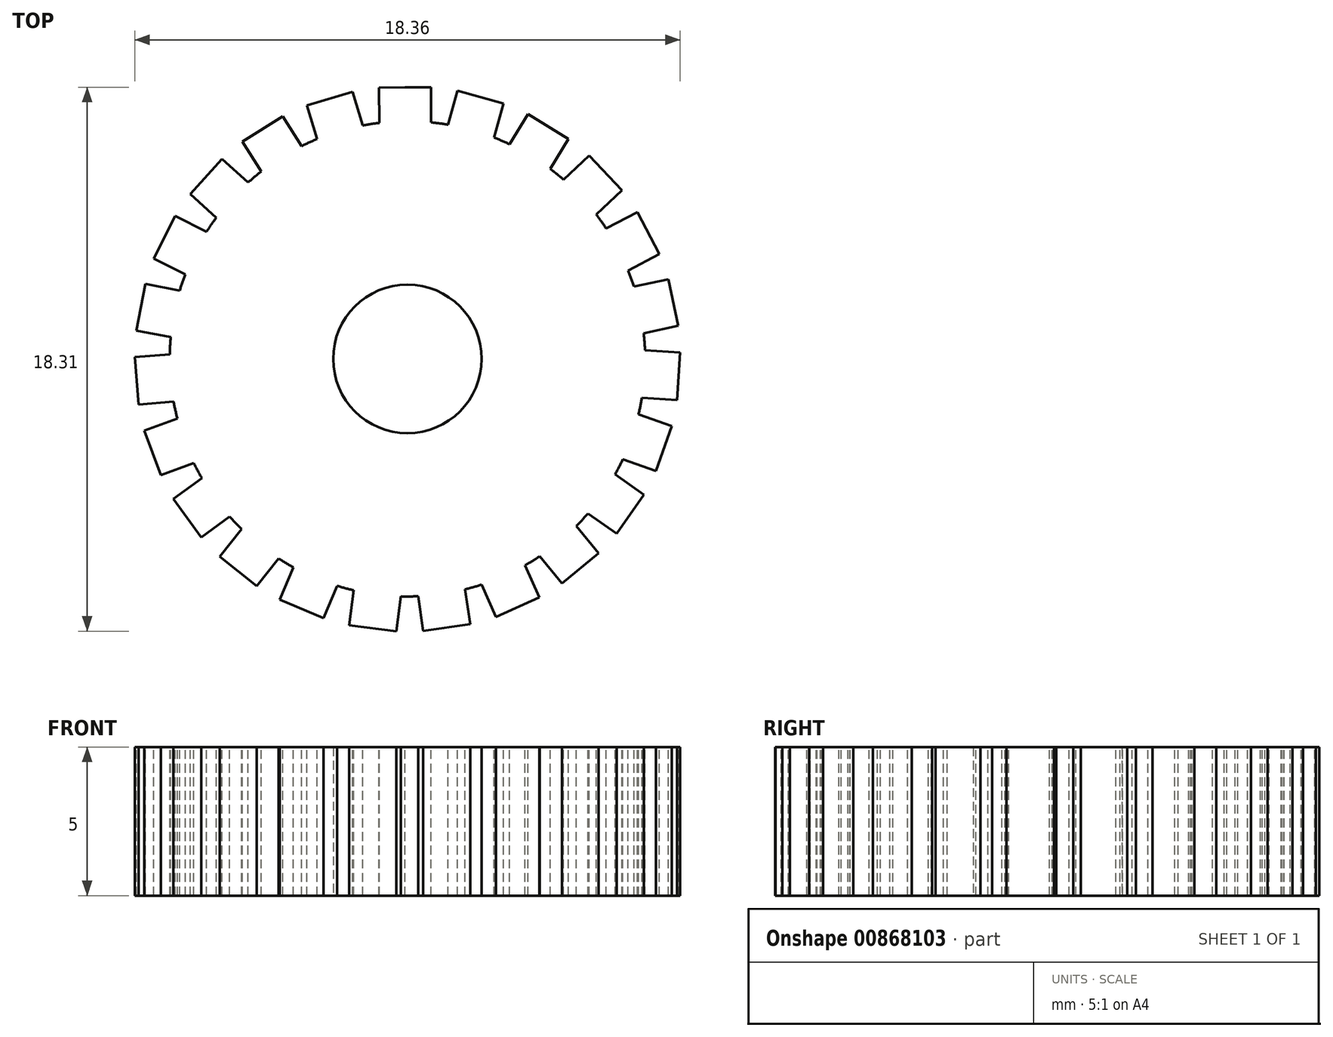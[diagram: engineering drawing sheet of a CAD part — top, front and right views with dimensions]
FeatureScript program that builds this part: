
annotation { "Feature Type Name" : "Feature", "Feature Type Description" : "" }
export const myFeature = defineFeature(function(context is Context, id is Id, definition is map)
    precondition{}
    {
        {
            var Q0;
            Q0=qCreatedBy(makeId("Top.planeOp"),FACE);
            var sketch = newSketch(context, id + "F0", { "sketchPlane" : qUnion([Q0])});
            skCircle(sketch, "E0", {"center": v(0, 0) * mm, "radius": 8 * mm});
            skCircle(sketch, "E1", {"center": v(0, 0) * mm, "radius": 2.5 * mm});
            skSolve(sketch);
        }
        {
            var Q0;
            Q0=makeQuery(id+"F0.imprint","IMPRINT",FACE,{"disambiguationData":[TD([[makeQuery(id+"F0.imprint","IMPRINT",EDGE,{"derivedFrom":sQuery(id+"F0.wireOp",EDGE,"E0")}),1.0]])]});
            extrude(context, id + "F1", {"entities" : qUnion([Q0]), "depth" : 5 * mm, "offsetDistance" : 25 * mm});
        }
        {
            var Q0;
            Q0=makeQuery(id+"F1.opExtrude","CAP_FACE",FACE,{"disambiguationData":[OSD([sQuery(id+"F0.wireOp",EDGE,"E0"),sQuery(id+"F0.wireOp",EDGE,"E1")])],"isStart":false});
            var sketch = newSketch(context, id + "F2", { "sketchPlane" : qUnion([Q0])});
            skLineSegment(sketch, "E2.bottom", {"start": v(-0.8, 9.14) * mm, "end": v(0.8, 9.14) * mm});
            skLineSegment(sketch, "E2.top", {"start": v(-0.8, 7.05) * mm, "end": v(0.8, 7.05) * mm});
            skLineSegment(sketch, "E2.right", {"start": v(0.8, 9.14) * mm, "end": v(0.8, 7.05) * mm});
            skLineSegment(sketch, "E3.1.0", {"start": v(3.23, 8.6) * mm, "end": v(2.67, 6.57) * mm});
            skLineSegment(sketch, "E3.1.1", {"start": v(1.69, 9.02) * mm, "end": v(3.23, 8.6) * mm});
            skLineSegment(sketch, "E3.1.2", {"start": v(1.69, 9.02) * mm, "end": v(1.13, 7) * mm});
            skLineSegment(sketch, "E3.1.3", {"start": v(1.13, 7) * mm, "end": v(2.67, 6.57) * mm});
            skLineSegment(sketch, "E3.2.0", {"start": v(5.42, 7.4) * mm, "end": v(4.34, 5.61) * mm});
            skLineSegment(sketch, "E3.2.1", {"start": v(4.06, 8.23) * mm, "end": v(5.42, 7.4) * mm});
            skLineSegment(sketch, "E3.2.2", {"start": v(4.06, 8.23) * mm, "end": v(2.97, 6.44) * mm});
            skLineSegment(sketch, "E3.2.3", {"start": v(2.97, 6.44) * mm, "end": v(4.34, 5.61) * mm});
            skLineSegment(sketch, "E3.3.0", {"start": v(7.22, 5.67) * mm, "end": v(5.69, 4.24) * mm});
            skLineSegment(sketch, "E3.3.1", {"start": v(6.12, 6.84) * mm, "end": v(7.22, 5.67) * mm});
            skLineSegment(sketch, "E3.3.2", {"start": v(6.12, 6.84) * mm, "end": v(4.6, 5.4) * mm});
            skLineSegment(sketch, "E3.3.3", {"start": v(4.6, 5.4) * mm, "end": v(5.69, 4.24) * mm});
            skLineSegment(sketch, "E3.4.0", {"start": v(8.48, 3.52) * mm, "end": v(6.62, 2.55) * mm});
            skLineSegment(sketch, "E3.4.1", {"start": v(7.74, 4.94) * mm, "end": v(8.48, 3.52) * mm});
            skLineSegment(sketch, "E3.4.2", {"start": v(7.74, 4.94) * mm, "end": v(5.88, 3.97) * mm});
            skLineSegment(sketch, "E3.4.3", {"start": v(5.88, 3.97) * mm, "end": v(6.62, 2.55) * mm});
            skLineSegment(sketch, "E3.5.0", {"start": v(9.11, 1.11) * mm, "end": v(7.06, 0.68) * mm});
            skLineSegment(sketch, "E3.5.1", {"start": v(8.78, 2.68) * mm, "end": v(9.11, 1.11) * mm});
            skLineSegment(sketch, "E3.5.2", {"start": v(8.78, 2.68) * mm, "end": v(6.73, 2.24) * mm});
            skLineSegment(sketch, "E3.5.3", {"start": v(6.73, 2.24) * mm, "end": v(7.06, 0.68) * mm});
            skLineSegment(sketch, "E3.6.0", {"start": v(9.07, -1.38) * mm, "end": v(6.98, -1.25) * mm});
            skLineSegment(sketch, "E3.6.1", {"start": v(9.18, 0.22) * mm, "end": v(9.07, -1.38) * mm});
            skLineSegment(sketch, "E3.6.2", {"start": v(9.18, 0.22) * mm, "end": v(7.08, 0.35) * mm});
            skLineSegment(sketch, "E3.6.3", {"start": v(7.08, 0.35) * mm, "end": v(6.98, -1.25) * mm});
            skLineSegment(sketch, "E3.7.0", {"start": v(8.37, -3.77) * mm, "end": v(6.39, -3.08) * mm});
            skLineSegment(sketch, "E3.7.1", {"start": v(8.9, -2.26) * mm, "end": v(8.37, -3.77) * mm});
            skLineSegment(sketch, "E3.7.2", {"start": v(8.9, -2.26) * mm, "end": v(6.92, -1.57) * mm});
            skLineSegment(sketch, "E3.7.3", {"start": v(6.92, -1.57) * mm, "end": v(6.39, -3.08) * mm});
            skLineSegment(sketch, "E3.8.0", {"start": v(7.04, -5.88) * mm, "end": v(5.32, -4.68) * mm});
            skLineSegment(sketch, "E3.8.1", {"start": v(7.96, -4.57) * mm, "end": v(7.04, -5.88) * mm});
            skLineSegment(sketch, "E3.8.2", {"start": v(7.96, -4.57) * mm, "end": v(6.24, -3.37) * mm});
            skLineSegment(sketch, "E3.8.3", {"start": v(6.24, -3.37) * mm, "end": v(5.32, -4.68) * mm});
            skLineSegment(sketch, "E3.9.0", {"start": v(5.2, -7.56) * mm, "end": v(3.87, -5.94) * mm});
            skLineSegment(sketch, "E3.9.1", {"start": v(6.44, -6.54) * mm, "end": v(5.2, -7.56) * mm});
            skLineSegment(sketch, "E3.9.2", {"start": v(6.44, -6.54) * mm, "end": v(5.1, -4.93) * mm});
            skLineSegment(sketch, "E3.9.3", {"start": v(5.1, -4.93) * mm, "end": v(3.87, -5.94) * mm});
            skLineSegment(sketch, "E3.10.0", {"start": v(2.98, -8.68) * mm, "end": v(2.12, -6.77) * mm});
            skLineSegment(sketch, "E3.10.1", {"start": v(4.44, -8.03) * mm, "end": v(2.98, -8.68) * mm});
            skLineSegment(sketch, "E3.10.2", {"start": v(4.44, -8.03) * mm, "end": v(3.59, -6.12) * mm});
            skLineSegment(sketch, "E3.10.3", {"start": v(3.59, -6.12) * mm, "end": v(2.12, -6.77) * mm});
            skLineSegment(sketch, "E3.11.0", {"start": v(0.53, -9.16) * mm, "end": v(0.23, -7.09) * mm});
            skLineSegment(sketch, "E3.11.1", {"start": v(2.11, -8.93) * mm, "end": v(0.53, -9.16) * mm});
            skLineSegment(sketch, "E3.11.2", {"start": v(2.11, -8.93) * mm, "end": v(1.8, -6.86) * mm});
            skLineSegment(sketch, "E3.11.3", {"start": v(1.8, -6.86) * mm, "end": v(0.23, -7.09) * mm});
            skLineSegment(sketch, "E3.12.0", {"start": v(-1.96, -8.97) * mm, "end": v(-1.69, -6.89) * mm});
            skLineSegment(sketch, "E3.12.1", {"start": v(-0.37, -9.17) * mm, "end": v(-1.96, -8.97) * mm});
            skLineSegment(sketch, "E3.12.2", {"start": v(-0.37, -9.17) * mm, "end": v(-0.1, -7.1) * mm});
            skLineSegment(sketch, "E3.12.3", {"start": v(-0.1, -7.1) * mm, "end": v(-1.69, -6.89) * mm});
            skLineSegment(sketch, "E3.13.0", {"start": v(-4.3, -8.11) * mm, "end": v(-3.48, -6.18) * mm});
            skLineSegment(sketch, "E3.13.1", {"start": v(-2.82, -8.73) * mm, "end": v(-4.3, -8.11) * mm});
            skLineSegment(sketch, "E3.13.2", {"start": v(-2.82, -8.73) * mm, "end": v(-2, -6.8) * mm});
            skLineSegment(sketch, "E3.13.3", {"start": v(-2, -6.8) * mm, "end": v(-3.48, -6.18) * mm});
            skLineSegment(sketch, "E3.14.0", {"start": v(-6.32, -6.66) * mm, "end": v(-5.01, -5.01) * mm});
            skLineSegment(sketch, "E3.14.1", {"start": v(-5.07, -7.65) * mm, "end": v(-6.32, -6.66) * mm});
            skLineSegment(sketch, "E3.14.2", {"start": v(-5.07, -7.65) * mm, "end": v(-3.76, -6.01) * mm});
            skLineSegment(sketch, "E3.14.3", {"start": v(-3.76, -6.01) * mm, "end": v(-5.01, -5.01) * mm});
            skLineSegment(sketch, "E3.15.0", {"start": v(-7.88, -4.7) * mm, "end": v(-6.18, -3.48) * mm});
            skLineSegment(sketch, "E3.15.1", {"start": v(-6.94, -6) * mm, "end": v(-7.88, -4.7) * mm});
            skLineSegment(sketch, "E3.15.2", {"start": v(-6.94, -6) * mm, "end": v(-5.24, -4.78) * mm});
            skLineSegment(sketch, "E3.15.3", {"start": v(-5.24, -4.78) * mm, "end": v(-6.18, -3.48) * mm});
            skLineSegment(sketch, "E3.16.0", {"start": v(-8.86, -2.42) * mm, "end": v(-6.89, -1.69) * mm});
            skLineSegment(sketch, "E3.16.1", {"start": v(-8.3, -3.92) * mm, "end": v(-8.86, -2.42) * mm});
            skLineSegment(sketch, "E3.16.2", {"start": v(-8.3, -3.92) * mm, "end": v(-6.33, -3.2) * mm});
            skLineSegment(sketch, "E3.16.3", {"start": v(-6.33, -3.2) * mm, "end": v(-6.89, -1.69) * mm});
            skLineSegment(sketch, "E3.17.0", {"start": v(-9.18, 0.06) * mm, "end": v(-7.09, 0.23) * mm});
            skLineSegment(sketch, "E3.17.1", {"start": v(-9.05, -1.54) * mm, "end": v(-9.18, 0.06) * mm});
            skLineSegment(sketch, "E3.17.2", {"start": v(-9.05, -1.54) * mm, "end": v(-6.96, -1.37) * mm});
            skLineSegment(sketch, "E3.17.3", {"start": v(-6.96, -1.37) * mm, "end": v(-7.09, 0.23) * mm});
            skLineSegment(sketch, "E3.18.0", {"start": v(-8.83, 2.52) * mm, "end": v(-6.77, 2.12) * mm});
            skLineSegment(sketch, "E3.18.1", {"start": v(-9.13, 0.95) * mm, "end": v(-8.83, 2.52) * mm});
            skLineSegment(sketch, "E3.18.2", {"start": v(-9.13, 0.95) * mm, "end": v(-7.07, 0.55) * mm});
            skLineSegment(sketch, "E3.18.3", {"start": v(-7.07, 0.55) * mm, "end": v(-6.77, 2.12) * mm});
            skLineSegment(sketch, "E3.19.0", {"start": v(-7.82, 4.8) * mm, "end": v(-5.94, 3.87) * mm});
            skLineSegment(sketch, "E3.19.1", {"start": v(-8.54, 3.37) * mm, "end": v(-7.82, 4.8) * mm});
            skLineSegment(sketch, "E3.19.2", {"start": v(-8.54, 3.37) * mm, "end": v(-6.66, 2.44) * mm});
            skLineSegment(sketch, "E3.19.3", {"start": v(-6.66, 2.44) * mm, "end": v(-5.94, 3.87) * mm});
            skLineSegment(sketch, "E3.20.0", {"start": v(-6.24, 6.73) * mm, "end": v(-4.68, 5.32) * mm});
            skLineSegment(sketch, "E3.20.1", {"start": v(-7.31, 5.55) * mm, "end": v(-6.24, 6.73) * mm});
            skLineSegment(sketch, "E3.20.2", {"start": v(-7.31, 5.55) * mm, "end": v(-5.76, 4.14) * mm});
            skLineSegment(sketch, "E3.20.3", {"start": v(-5.76, 4.14) * mm, "end": v(-4.68, 5.32) * mm});
            skLineSegment(sketch, "E3.21.0", {"start": v(-4.2, 8.16) * mm, "end": v(-3.08, 6.39) * mm});
            skLineSegment(sketch, "E3.21.1", {"start": v(-5.55, 7.3) * mm, "end": v(-4.2, 8.16) * mm});
            skLineSegment(sketch, "E3.21.2", {"start": v(-5.55, 7.3) * mm, "end": v(-4.43, 5.53) * mm});
            skLineSegment(sketch, "E3.21.3", {"start": v(-4.43, 5.53) * mm, "end": v(-3.08, 6.39) * mm});
            skLineSegment(sketch, "E3.22.0", {"start": v(-1.85, 9) * mm, "end": v(-1.25, 6.98) * mm});
            skLineSegment(sketch, "E3.22.1", {"start": v(-3.38, 8.53) * mm, "end": v(-1.85, 9) * mm});
            skLineSegment(sketch, "E3.22.2", {"start": v(-3.38, 8.53) * mm, "end": v(-2.78, 6.52) * mm});
            skLineSegment(sketch, "E3.22.3", {"start": v(-2.78, 6.52) * mm, "end": v(-1.25, 6.98) * mm});
            skLineSegment(sketch, "E3.23.1", {"start": v(-0.96, 9.13) * mm, "end": v(0.64, 9.16) * mm});
            skLineSegment(sketch, "E3.23.2", {"start": v(-0.96, 9.13) * mm, "end": v(-0.92, 7.03) * mm});
            skLineSegment(sketch, "E3.23.3", {"start": v(-0.92, 7.03) * mm, "end": v(0.68, 7.06) * mm});
            skPoint(sketch, "E3.center", {"position": v(0, 0) * mm});
            skLineSegment(sketch, "E3.anchor1", {"start": v(0, 0) * mm, "end": v(-0.8, 7.05) * mm, "construction": true});
            skLineSegment(sketch, "E3.anchor2", {"start": v(0, 0) * mm, "end": v(-0.92, 7.03) * mm, "construction": true});
            skSolve(sketch);
        }
        {
            var Q0;
            {var subQ0=sQuery(id+"F2.wireOp",EDGE,"E3.19.1");Q0=makeQuery(id+"F2.imprint","IMPRINT",FACE,{"disambiguationData":[TD([[makeQuery(id+"F2.imprint","IMPRINT",EDGE,{"derivedFrom":subQ0}),-1.0]])]});}
            var Q1;
            {var subQ0=sQuery(id+"F2.wireOp",EDGE,"E3.18.1");Q1=makeQuery(id+"F2.imprint","IMPRINT",FACE,{"disambiguationData":[TD([[makeQuery(id+"F2.imprint","IMPRINT",EDGE,{"derivedFrom":subQ0}),-1.0]])]});}
            var Q2;
            {var subQ0=sQuery(id+"F2.wireOp",EDGE,"E3.17.1");Q2=makeQuery(id+"F2.imprint","IMPRINT",FACE,{"disambiguationData":[TD([[makeQuery(id+"F2.imprint","IMPRINT",EDGE,{"derivedFrom":subQ0}),-1.0]])]});}
            var Q3;
            {var subQ0=sQuery(id+"F2.wireOp",EDGE,"E3.16.1");Q3=makeQuery(id+"F2.imprint","IMPRINT",FACE,{"disambiguationData":[TD([[makeQuery(id+"F2.imprint","IMPRINT",EDGE,{"derivedFrom":subQ0}),-1.0]])]});}
            var Q4;
            {var subQ0=sQuery(id+"F2.wireOp",EDGE,"E3.15.1");Q4=makeQuery(id+"F2.imprint","IMPRINT",FACE,{"disambiguationData":[TD([[makeQuery(id+"F2.imprint","IMPRINT",EDGE,{"derivedFrom":subQ0}),-1.0]])]});}
            var Q5;
            {var subQ0=sQuery(id+"F2.wireOp",EDGE,"E3.14.1");Q5=makeQuery(id+"F2.imprint","IMPRINT",FACE,{"disambiguationData":[TD([[makeQuery(id+"F2.imprint","IMPRINT",EDGE,{"derivedFrom":subQ0}),-1.0]])]});}
            var Q6;
            {var subQ0=sQuery(id+"F2.wireOp",EDGE,"E3.13.1");Q6=makeQuery(id+"F2.imprint","IMPRINT",FACE,{"disambiguationData":[TD([[makeQuery(id+"F2.imprint","IMPRINT",EDGE,{"derivedFrom":subQ0}),-1.0]])]});}
            var Q7;
            {var subQ0=sQuery(id+"F2.wireOp",EDGE,"E3.12.1");Q7=makeQuery(id+"F2.imprint","IMPRINT",FACE,{"disambiguationData":[TD([[makeQuery(id+"F2.imprint","IMPRINT",EDGE,{"derivedFrom":subQ0}),-1.0]])]});}
            var Q8;
            {var subQ0=sQuery(id+"F2.wireOp",EDGE,"E3.11.1");Q8=makeQuery(id+"F2.imprint","IMPRINT",FACE,{"disambiguationData":[TD([[makeQuery(id+"F2.imprint","IMPRINT",EDGE,{"derivedFrom":subQ0}),-1.0]])]});}
            var Q9;
            {var subQ0=sQuery(id+"F2.wireOp",EDGE,"E3.10.1");Q9=makeQuery(id+"F2.imprint","IMPRINT",FACE,{"disambiguationData":[TD([[makeQuery(id+"F2.imprint","IMPRINT",EDGE,{"derivedFrom":subQ0}),-1.0]])]});}
            var Q10;
            {var subQ0=sQuery(id+"F2.wireOp",EDGE,"E3.9.1");Q10=makeQuery(id+"F2.imprint","IMPRINT",FACE,{"disambiguationData":[TD([[makeQuery(id+"F2.imprint","IMPRINT",EDGE,{"derivedFrom":subQ0}),-1.0]])]});}
            var Q11;
            {var subQ0=sQuery(id+"F2.wireOp",EDGE,"E3.8.1");Q11=makeQuery(id+"F2.imprint","IMPRINT",FACE,{"disambiguationData":[TD([[makeQuery(id+"F2.imprint","IMPRINT",EDGE,{"derivedFrom":subQ0}),-1.0]])]});}
            var Q12;
            {var subQ0=sQuery(id+"F2.wireOp",EDGE,"E3.7.1");Q12=makeQuery(id+"F2.imprint","IMPRINT",FACE,{"disambiguationData":[TD([[makeQuery(id+"F2.imprint","IMPRINT",EDGE,{"derivedFrom":subQ0}),-1.0]])]});}
            var Q13;
            {var subQ0=sQuery(id+"F2.wireOp",EDGE,"E3.6.1");Q13=makeQuery(id+"F2.imprint","IMPRINT",FACE,{"disambiguationData":[TD([[makeQuery(id+"F2.imprint","IMPRINT",EDGE,{"derivedFrom":subQ0}),-1.0]])]});}
            var Q14;
            {var subQ0=sQuery(id+"F2.wireOp",EDGE,"E3.5.1");Q14=makeQuery(id+"F2.imprint","IMPRINT",FACE,{"disambiguationData":[TD([[makeQuery(id+"F2.imprint","IMPRINT",EDGE,{"derivedFrom":subQ0}),-1.0]])]});}
            var Q15;
            {var subQ0=sQuery(id+"F2.wireOp",EDGE,"E3.4.1");Q15=makeQuery(id+"F2.imprint","IMPRINT",FACE,{"disambiguationData":[TD([[makeQuery(id+"F2.imprint","IMPRINT",EDGE,{"derivedFrom":subQ0}),-1.0]])]});}
            var Q16;
            {var subQ0=sQuery(id+"F2.wireOp",EDGE,"E3.3.1");Q16=makeQuery(id+"F2.imprint","IMPRINT",FACE,{"disambiguationData":[TD([[makeQuery(id+"F2.imprint","IMPRINT",EDGE,{"derivedFrom":subQ0}),-1.0]])]});}
            var Q17;
            {var subQ0=sQuery(id+"F2.wireOp",EDGE,"E3.2.1");Q17=makeQuery(id+"F2.imprint","IMPRINT",FACE,{"disambiguationData":[TD([[makeQuery(id+"F2.imprint","IMPRINT",EDGE,{"derivedFrom":subQ0}),-1.0]])]});}
            var Q18;
            {var subQ0=sQuery(id+"F2.wireOp",EDGE,"E3.1.1");Q18=makeQuery(id+"F2.imprint","IMPRINT",FACE,{"disambiguationData":[TD([[makeQuery(id+"F2.imprint","IMPRINT",EDGE,{"derivedFrom":subQ0}),-1.0]])]});}
            var Q19;
            {var subQ3=sQuery(id+"F2.wireOp",EDGE,"E2.bottom");var subQ7=sQuery(id+"F2.wireOp",EDGE,"E2.right");var subQ8=makeQuery(id+"F2.imprint","INTERSECT",VERTEX,{"derivedFrom":[subQ3,subQ7]});Q19=makeQuery(id+"F2.imprint","IMPRINT",FACE,{"disambiguationData":[TD([[makeQuery(id+"F2.imprint","IMPRINT",EDGE,{"disambiguationData":[TD([[subQ8,1.0]])],"derivedFrom":subQ3}),-1.0]])]});}
            var Q20;
            {var subQ0=sQuery(id+"F2.wireOp",EDGE,"E3.21.1");Q20=makeQuery(id+"F2.imprint","IMPRINT",FACE,{"disambiguationData":[TD([[makeQuery(id+"F2.imprint","IMPRINT",EDGE,{"derivedFrom":subQ0}),-1.0]])]});}
            var Q21;
            {var subQ0=sQuery(id+"F2.wireOp",EDGE,"E3.20.1");Q21=makeQuery(id+"F2.imprint","IMPRINT",FACE,{"disambiguationData":[TD([[makeQuery(id+"F2.imprint","IMPRINT",EDGE,{"derivedFrom":subQ0}),-1.0]])]});}
            var Q22;
            {var subQ0=sQuery(id+"F2.wireOp",EDGE,"E3.22.1");Q22=makeQuery(id+"F2.imprint","IMPRINT",FACE,{"disambiguationData":[TD([[makeQuery(id+"F2.imprint","IMPRINT",EDGE,{"derivedFrom":subQ0}),-1.0]])]});}
            extrude(context, id + "F3", {"entities" : qUnion([Q0, Q1, Q2, Q3, Q4, Q5, Q6, Q7, Q8, Q9, Q10, Q11, Q12, Q13, Q14, Q15, Q16, Q17, Q18, Q19, Q20, Q21, Q22]), "operationType" : NewBodyOperationType.ADD, "oppositeDirection" : true, "depth" : 5 * mm, "offsetDistance" : 25 * mm});
        }
    });
